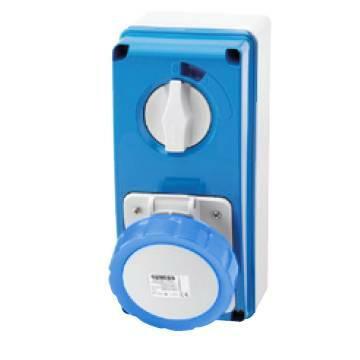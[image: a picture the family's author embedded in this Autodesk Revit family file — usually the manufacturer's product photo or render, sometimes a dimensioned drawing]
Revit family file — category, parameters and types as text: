
# Revit family: Building-IEC309Connections-GEWISS-67IB-INTERLOCKED-SOCKET-OUTLETS_IP67_WITH_BOTTOM
name_source: partatom
category: Apparecchi elettrici
revit_build: Autodesk Revit 2016 (Build: 20161004_0715(x64)
units: mm (PartAtom-declared; Revit-internal decimal feet)

## family parameters
Condiviso = No
Host = Muro
Mantenere orientamento annotazione = Sì
Numero OmniClass = 23.80.50.14
Punto di calcolo locali = No
Quota connettore circolare = Usa diametro
Sempre verticale = Sì
Taglio con vuoti quando caricato = No
Tipo di parte = Normale
Titolo OmniClass = Plug Connectors

## types (23) — shared parameters
Altezza da terra = 1112 mm
Carico apparente = 0 VA
Catalogue = BUILDING
Catalogue Range = 67 IB
Classificazione carico = Altro
Electrocod = 2222
Frequency = 50/60 Hz
Glow Wire Test = 850 °C (IB socket) - 650 °C (bottom)
Glow wire test: = 850 °C (IB socket) - 650 °C (bottom)
IDF = c396004b-a83b-4ac0-a4fa-669de3df814d
IDT = 80fd8aa3-f4ad-4bf9-871a-178f60767a59
IP degree = IP67
Immagine tipo = GW66207N.jpg
Numero poli = 3
Operating temperature: = -25 +40 °C
Potenza = 400 V
Presa = GW - ROSSO
Produttore = GEWISS S.p.A.
Protection = NO (SBF)
Rated frequency (Hz) = 50/60 Hz
SEO = Socket outlet
Shock resistance = IK08
Struttura = GEWISS - Grigio RAL - 7035
Struttura frontale = GEWISS -BLU
Technical sheet = https://www.gewiss.com
Thermo-pressure with ball = 125 °C (IB socket) - 80 °C (bottom)
Tipo Simbolo = PRESAINDSTAGNA : 3P
Typology = Vertical
URL = https://www.gewiss.com
Version file RFA = 18.0
Vetro = GEWISS - vetro
With back-mounting box = Yes
Working temperature = -25 ÷ +40 °C

## per-type parameters (varying)
| type | Colour | Colour: | Descrizione | EAN code | Modello | No. of poles | Number of poles | Rated current (A) | Rated current (In) | Rated voltage | Rated voltage: | Reference h |
| GW66221N - 32A 3P+E 500V V.INT.SOCK.O.W.B.7H SBF | Black | Black | 32A 3P+E 500V V.INT.SOCK.O.W.B.7H SBF | 8011564741317 | GW66221N | 3P+E | 3P+E | 32 | 32 | 480 - 500 V | 480 - 500 V | 7 |
| GW66201N - 16A 2P+E 110V V.INT.SOCK.O.W.B.4H SBF | Yellow | Yellow | 16A 2P+E 110V V.INT.SOCK.O.W.B.4H SBF | 8011564741140 | GW66201N | 2P+E | 2P+E | 16 | 16 | 100 - 130 V | 100 - 130 V | 4 |
| GW66257N - 32A 3P+E 380V V.INT.SOCK.O.W.B.3H SBF | Red | Red | 32A 3P+E 380V V.INT.SOCK.O.W.B.3H SBF | 8011564741522 | GW66257N | 3P+E | 3P+E | 32 | 32 | 380 - 440 V | 380 - 440 V | 3 |
| GW66222N - 32A 3P+N+E 500V V.INT.SOCK.O.W.B.7H SBF | Black | Black | 32A 3P+N+E 500V V.INT.SOCK.O.W.B.7H SBF | 8011564741324 | GW66222N | 3P+N+E | 3P+N+E | 32 | 32 | 480 - 500 V | 480 - 500 V | 7 |
| GW66206N - 16A 3P+N+E 230V V.INT.SOCK.O.W.B.9H SBF | Blue | Blue | 16A 3P+N+E 230V V.INT.SOCK.O.W.B.9H SBF | 8011564741195 | GW66206N | 3P+N+E | 3P+N+E | 16 | 16 | 200 - 250 V | 200 - 250 V | 9 |
| GW66214N - 32A 3P+N+E 110V V.INT.SOCK.O.W.B.4H SBF | Yellow | Yellow | 32A 3P+N+E 110V V.INT.SOCK.O.W.B.4H SBF | 8011564741263 | GW66214N | 3P+N+E | 3P+N+E | 32 | 32 | 100 - 130 V | 100 - 130 V | 4 |
| GW66216N - 32A 3P+E 230V V.INT.SOCK.O.W.B.9H SBF | Blue | Blue | 32A 3P+E 230V V.INT.SOCK.O.W.B.9H SBF | 8011564741270 | GW66216N | 3P+E | 3P+E | 32 | 32 | 200 - 250 V | 200 - 250 V | 9 |
| GW66208N - 16A 3P+E 400V V.INT.SOCK.O.W.B.6H SBF | Red | Red | 16A 3P+E 400V V.INT.SOCK.O.W.B.6H SBF | 8011564741218 | GW66208N | 3P+E | 3P+E | 16 | 16 | 380 - 415 V | 380 - 415 V | 6 |
| GW66220N - 32A 3P+N+E 400V V.INT.SOCK.O.W.B.6H SBF | Red | Red | 32A 3P+N+E 400V V.INT.SOCK.O.W.B.6H SBF | 8011564742536 | GW66220N | 3P+N+E | 3P+N+E | 32 | 32 | 380 - 415 V | 380 - 415 V | 6 |
| GW66202N - 16A 3P+E 110V V.INT.SOCK.O.W.B.4H SBF | Yellow | Yellow | 16A 3P+E 110V V.INT.SOCK.O.W.B.4H SBF | 8011564741157 | GW66202N | 3P+E | 3P+E | 16 | 16 | 100 - 130 V | 100 - 130 V | 4 |
| GW66203N - 16A 3P+N+E 110V V.INT.SOCK.O.W.B.4H SBF | Yellow | Yellow | 16A 3P+N+E 110V V.INT.SOCK.O.W.B.4H SBF | 8011564741164 | GW66203N | 3P+N+E | 3P+N+E | 16 | 16 | 100 - 130 V | 100 - 130 V | 4 |
| GW66207N - 16A 2P+E 400V V.INT.SOCK.O.W.B.9H SBF | Red | Red | 16A 2P+E 400V V.INT.SOCK.O.W.B.9H SBF | 8011564741201 | GW66207N | 2P+E | 2P+E | 16 | 16 | 380 - 415 V | 380 - 415 V | 9 |
| GW66210N - 16A 3P+E 500V V.INT.SOCK.O.W.B.7H SBF | Black | Black | 16A 3P+E 500V V.INT.SOCK.O.W.B.7H SBF | 8011564741225 | GW66210N | 3P+E | 3P+E | 16 | 16 | 480 - 500 V | 480 - 500 V | 7 |
| GW66211N - 16A 3P+N+E 500V V.INT.SOCK.O.W.B.7H SBF | Black | Black | 16A 3P+N+E 500V V.INT.SOCK.O.W.B.7H SBF | 8011564741232 | GW66211N | 3P+N+E | 3P+N+E | 16 | 16 | 480 - 500 V | 480 - 500 V | 7 |
| GW66204N - 16A 2P+E 230V V.INT.SOCK.O.W.B.6H SBF | Blue | Blue | 16A 2P+E 230V V.INT.SOCK.O.W.B.6H SBF | 8011564741171 | GW66204N | 2P+E | 2P+E | 16 | 16 | 200 - 250 V | 200 - 250 V | 6 |
| GW66218N - 32A 2P+E 400V V.INT.SOCK.O.W.B.9H SBF | Red | Red | 32A 2P+E 400V V.INT.SOCK.O.W.B.9H SBF | 8011564741294 | GW66218N | 2P+E | 2P+E | 32 | 32 | 380 - 415 V | 380 - 415 V | 9 |
| GW66213N - 32A 3P+E 110V V.INT.SOCK.O.W.B.4H SBF | Yellow | Yellow | 32A 3P+E 110V V.INT.SOCK.O.W.B.4H SBF | 8011564741256 | GW66213N | 3P+E | 3P+E | 32 | 32 | 100 - 130 V | 100 - 130 V | 4 |
| GW66215N - 32A 2P+E 230V V.INT.SOCK.O.W.B.6H SBF | Blue | Blue | 32A 2P+E 230V V.INT.SOCK.O.W.B.6H SBF | 8011564742529 | GW66215N | 2P+E | 2P+E | 32 | 32 | 200 - 250 V | 200 - 250 V | 6 |
| GW66217N - 32A 3P+N+E 230V V.INT.SOCK.O.W.B.9H SBF | Blue | Blue | 32A 3P+N+E 230V V.INT.SOCK.O.W.B.9H SBF | 8011564741287 | GW66217N | 3P+N+E | 3P+N+E | 32 | 32 | 200 - 250 V | 200 - 250 V | 9 |
| GW66212N - 32A 2P+E 110V V.INT.SOCK.O.W.B.4H SBF | Yellow | Yellow | 32A 2P+E 110V V.INT.SOCK.O.W.B.4H SBF | 8011564741249 | GW66212N | 2P+E | 2P+E | 32 | 32 | 100 - 130 V | 100 - 130 V | 4 |
| GW66205N - 16A 3P+E 230V V.INT.SOCK.O.W.B.9H SBF | Blue | Blue | 16A 3P+E 230V V.INT.SOCK.O.W.B.9H SBF | 8011564741188 | GW66205N | 3P+E | 3P+E | 16 | 16 | 200 - 250 V | 200 - 250 V | 9 |
| GW66219N - 32A 3P+E 400V V.INT.SOCK.O.W.B.6H SBF | Red | Red | 32A 3P+E 400V V.INT.SOCK.O.W.B.6H SBF | 8011564741300 | GW66219N | 3P+E | 3P+E | 32 | 32 | 380 - 415 V | 380 - 415 V | 6 |
| GW66209N - 16A 3P+N+E 400V V.INT.SOCK.O.W.B.6H SBF | Red | Red | 16A 3P+N+E 400V V.INT.SOCK.O.W.B.6H SBF | 8011564742512 | GW66209N | 3P+N+E | 3P+N+E | 16 | 16 | 380 - 415 V | 380 - 415 V | 6 |

## geometry (parser evidence)
native form markers: Sweep x1
no freeform markers — native parametric forms only
